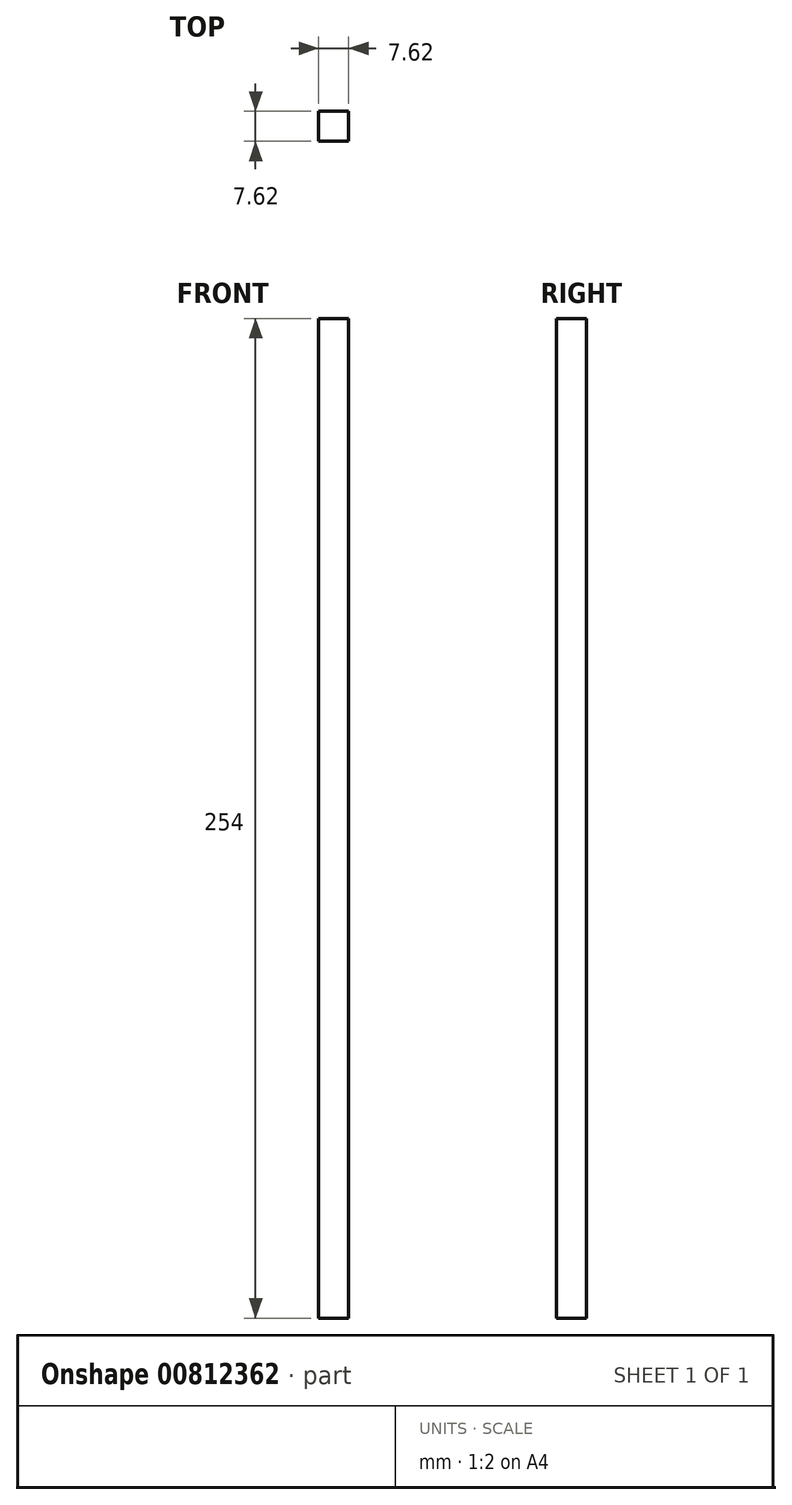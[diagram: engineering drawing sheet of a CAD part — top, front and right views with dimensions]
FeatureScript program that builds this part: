
annotation { "Feature Type Name" : "Feature", "Feature Type Description" : "" }
export const myFeature = defineFeature(function(context is Context, id is Id, definition is map)
    precondition{}
    {
        {
            var Q0;
            Q0=qCreatedBy(makeId("Top.planeOp"),FACE);
            var sketch = newSketch(context, id + "F0", { "sketchPlane" : qUnion([Q0])});
            skLineSegment(sketch, "E0.bottom", {"start": v(3.8, -3.8) * mm, "end": v(-3.81, -3.81) * mm});
            skLineSegment(sketch, "E0.top", {"start": v(3.81, 3.81) * mm, "end": v(-3.8, 3.8) * mm});
            skLineSegment(sketch, "E0.left", {"start": v(3.8, -3.8) * mm, "end": v(3.81, 3.81) * mm});
            skLineSegment(sketch, "E0.right", {"start": v(-3.81, -3.81) * mm, "end": v(-3.8, 3.8) * mm});
            skPoint(sketch, "E0.middle", {"position": v(0, 0) * mm});
            skSolve(sketch);
        }
        {
            var Q0;
            Q0=makeQuery(id+"F0.imprint","IMPRINT",FACE,{"disambiguationData":[TD([[makeQuery(id+"F0.imprint","IMPRINT",EDGE,{"derivedFrom":sQuery(id+"F0.wireOp",EDGE,"E0.bottom")}),-1.0]])]});
            extrude(context, id + "F1", {"entities" : qUnion([Q0]), "depth" : 254 * mm, "offsetDistance" : 25.4 * mm});
        }
    });
